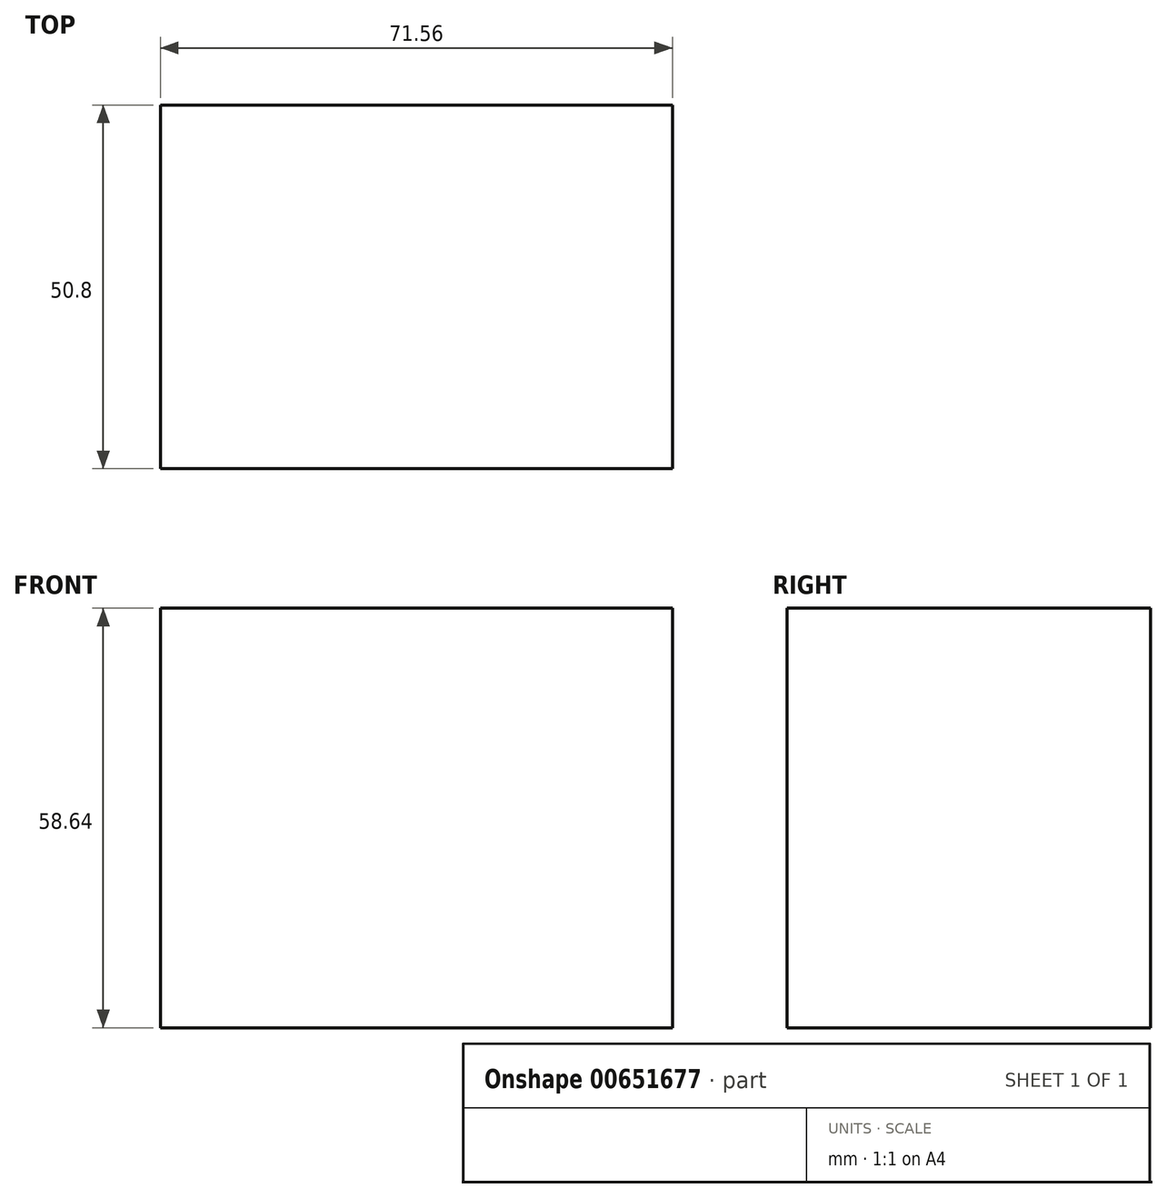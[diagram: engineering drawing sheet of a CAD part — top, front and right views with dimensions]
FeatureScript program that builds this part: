
annotation { "Feature Type Name" : "Feature", "Feature Type Description" : "" }
export const myFeature = defineFeature(function(context is Context, id is Id, definition is map)
    precondition{}
    {
        {
            var Q0;
            Q0=qCreatedBy(makeId("Front.planeOp"),FACE);
            var sketch = newSketch(context, id + "F0", { "sketchPlane" : qUnion([Q0])});
            skLineSegment(sketch, "E0.bottom", {"start": v(35.78, 29.32) * mm, "end": v(-35.78, 29.32) * mm});
            skLineSegment(sketch, "E0.top", {"start": v(35.78, -29.32) * mm, "end": v(-35.78, -29.32) * mm});
            skLineSegment(sketch, "E0.left", {"start": v(35.78, 29.32) * mm, "end": v(35.78, -29.32) * mm});
            skLineSegment(sketch, "E0.right", {"start": v(-35.78, 29.32) * mm, "end": v(-35.78, -29.32) * mm});
            skPoint(sketch, "E0.middle", {"position": v(0, 0) * mm});
            skLineSegment(sketch, "E1.bottom", {"start": v(18.81, 29.32) * mm, "end": v(-18.81, 29.32) * mm});
            skLineSegment(sketch, "E1.top", {"start": v(18.81, 61.78) * mm, "end": v(-18.81, 61.78) * mm});
            skLineSegment(sketch, "E1.left", {"start": v(18.81, 29.32) * mm, "end": v(18.81, 61.78) * mm});
            skLineSegment(sketch, "E1.right", {"start": v(-18.81, 29.32) * mm, "end": v(-18.81, 61.78) * mm});
            skPoint(sketch, "E1.middle", {"position": v(0, 45.55) * mm});
            skSolve(sketch);
        }
        {
            var Q0;
            Q0=makeQuery(id+"F0.imprint","IMPRINT",FACE,{"disambiguationData":[TD([[makeQuery(id+"F0.imprint","IMPRINT",EDGE,{"derivedFrom":sQuery(id+"F0.wireOp",EDGE,"E0.top")}),-1.0]])]});
            extrude(context, id + "F1", {"entities" : qUnion([Q0]), "depth" : 50.8 * mm, "offsetDistance" : 25.4 * mm});
        }
    });
